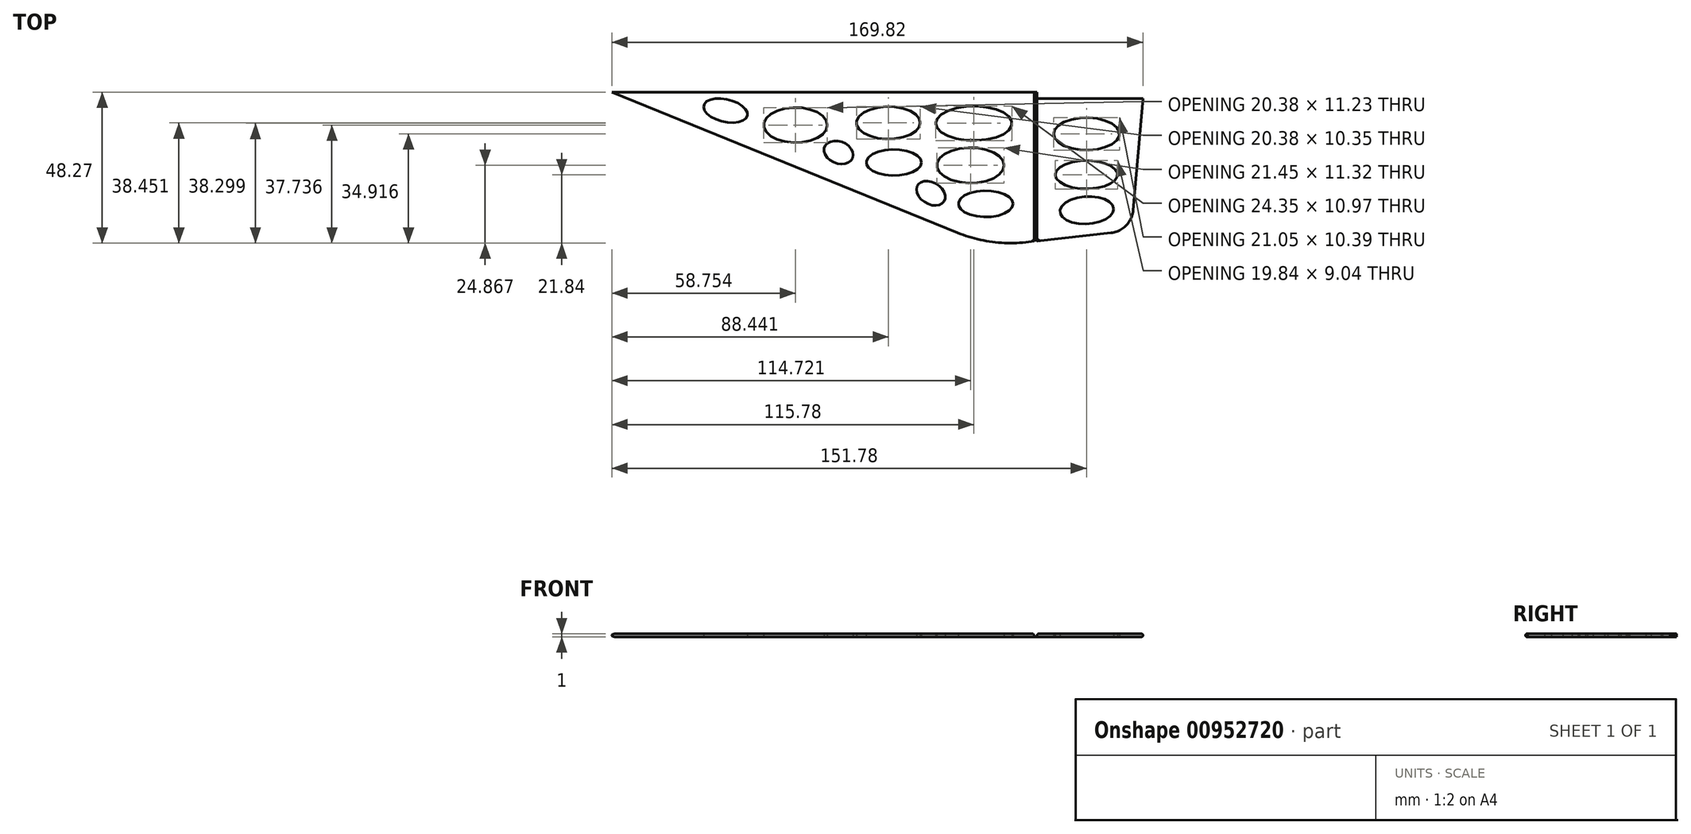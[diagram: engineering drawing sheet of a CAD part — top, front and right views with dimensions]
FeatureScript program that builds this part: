
annotation { "Feature Type Name" : "Feature", "Feature Type Description" : "" }
export const myFeature = defineFeature(function(context is Context, id is Id, definition is map)
    precondition{}
    {
        {
            var Q0;
            Q0=qCreatedBy(makeId("Top.planeOp"),FACE);
            var sketch = newSketch(context, id + "F0", { "sketchPlane" : qUnion([Q0])});
            skLineSegment(sketch, "E0", {"start": v(-90.21, 0) * mm, "end": v(44.79, 0) * mm});
            skLineSegment(sketch, "E1", {"start": v(76.47, -37.77) * mm, "end": v(79.61, -2) * mm});
            skLineSegment(sketch, "E2", {"start": v(-90.21, 0) * mm, "end": v(20.3, -44.95) * mm});
            skLineSegment(sketch, "E3", {"start": v(42.13, -48) * mm, "end": v(69.37, -45.03) * mm});
            skArc(sketch, "E4.filletArc", {"start": v(20.3, -44.95) * mm, "mid": v(31.02, -47.83) * mm, "end": v(42.13, -48) * mm});
            skArc(sketch, "E5.filletArc", {"start": v(69.37, -45.03) * mm, "mid": v(74.22, -42.67) * mm, "end": v(76.47, -37.77) * mm});
            skLineSegment(sketch, "E6", {"start": v(45.79, -2) * mm, "end": v(45.79, -47.6) * mm});
            skLineSegment(sketch, "E7.0", {"start": v(44.79, 0) * mm, "end": v(44.79, -47.7) * mm});
            skLineSegment(sketch, "E8.trimOffspring", {"start": v(45.79, -2) * mm, "end": v(79.61, -2) * mm});
            skPoint(sketch, "E9.orphan", {"position": v(45.79, 0) * mm});
            skPoint(sketch, "E10.orphan", {"position": v(79.79, 0) * mm});
            skLineSegment(sketch, "E11", {"start": v(44.79, 0) * mm, "end": v(45.79, 0) * mm});
            skLineSegment(sketch, "E12", {"start": v(45.79, -2) * mm, "end": v(45.79, 0) * mm});
            skEllipse(sketch, "E13", {"center": v(61.57, -13.35) * mm, "majorRadius": 10.52 * mm, "minorRadius": 5.2 * mm, "majorAxis": v(-1, 0)});
            skEllipse(sketch, "E14", {"center": v(61.57, -26.43) * mm, "majorRadius": 9.92 * mm, "minorRadius": 4.52 * mm, "majorAxis": v(-1, 0)});
            skEllipse(sketch, "E15", {"center": v(61.65, -37.78) * mm, "majorRadius": 8.57 * mm, "minorRadius": 4.4 * mm, "majorAxis": v(1, 0.06)});
            skEllipse(sketch, "E16", {"center": v(25.57, -9.97) * mm, "majorRadius": 12.18 * mm, "minorRadius": 5.48 * mm, "majorAxis": v(-1, 0)});
            skEllipse(sketch, "E17", {"center": v(24.51, -23.4) * mm, "majorRadius": 10.73 * mm, "minorRadius": 5.66 * mm, "majorAxis": v(1, 0)});
            skEllipse(sketch, "E18", {"center": v(29.34, -35.74) * mm, "majorRadius": 8.76 * mm, "minorRadius": 4.21 * mm, "majorAxis": v(1, 0)});
            skEllipse(sketch, "E19", {"center": v(-1.77, -9.82) * mm, "majorRadius": 10.2 * mm, "minorRadius": 5.17 * mm, "majorAxis": v(1, 0)});
            skEllipse(sketch, "E20", {"center": v(0, -22.5) * mm, "majorRadius": 8.82 * mm, "minorRadius": 4.16 * mm, "majorAxis": v(1, 0)});
            skEllipse(sketch, "E21", {"center": v(11.82, -32.34) * mm, "majorRadius": 4.98 * mm, "minorRadius": 3.47 * mm, "majorAxis": v(0.85, -0.52)});
            skEllipse(sketch, "E22", {"center": v(-31.46, -10.53) * mm, "majorRadius": 10.2 * mm, "minorRadius": 5.62 * mm, "majorAxis": v(1, 0)});
            skEllipse(sketch, "E23", {"center": v(-17.68, -19.3) * mm, "majorRadius": 4.81 * mm, "minorRadius": 3.52 * mm, "majorAxis": v(0.93, -0.37)});
            skEllipse(sketch, "E24", {"center": v(-53.82, -5.89) * mm, "majorRadius": 7.16 * mm, "minorRadius": 3.62 * mm, "majorAxis": v(0.97, -0.22)});
            skSolve(sketch);
        }
        {
            var Q0;
            Q0=makeQuery(id+"F0.imprint","IMPRINT",FACE,{"disambiguationData":[TD([[makeQuery(id+"F0.imprint","IMPRINT",EDGE,{"derivedFrom":sQuery(id+"F0.wireOp",EDGE,"E0")}),-1.0]])]});
            var Q1;
            {var subQ0=sQuery(id+"F0.wireOp",EDGE,"E6");Q1=makeQuery(id+"F0.imprint","IMPRINT",FACE,{"disambiguationData":[TD([[makeQuery(id+"F0.imprint","IMPRINT",EDGE,{"derivedFrom":subQ0}),-1.0]])]});}
            var Q2;
            Q2=makeQuery(id+"F0.imprint","IMPRINT",FACE,{"disambiguationData":[TD([[makeQuery(id+"F0.imprint","IMPRINT",EDGE,{"derivedFrom":sQuery(id+"F0.wireOp",EDGE,"E1")}),1.0]])]});
            extrude(context, id + "F1", {"entities" : qUnion([Q0, Q1, Q2]), "depth" : 1 * mm, "offsetDistance" : 25 * mm});
        }
        {
            var Q0;
            {var subQ0=sQuery(id+"F0.wireOp",EDGE,"E6");Q0=makeQuery(id+"F0.imprint","IMPRINT",FACE,{"disambiguationData":[TD([[makeQuery(id+"F0.imprint","IMPRINT",EDGE,{"derivedFrom":subQ0}),-1.0]])]});}
            extrude(context, id + "F2", {"entities" : qUnion([Q0]), "operationType" : NewBodyOperationType.REMOVE, "depth" : 2 * mm, "offsetDistance" : 25 * mm, "hasSecondDirection" : true, "secondDirectionOppositeDirection" : false, "secondDirectionDepth" : 0.15 * mm});
        }
        {
            var Q0;
            Q0=makeQuery(id+"F1.opExtrude","CAP_EDGE",EDGE,{"disambiguationData":[OSD([sQuery(id+"F0.wireOp",EDGE,"E2")])],"isStart":true});
            var Q1;
            Q1=makeQuery(id+"F1.opExtrude","CAP_EDGE",EDGE,{"disambiguationData":[OSD([sQuery(id+"F0.wireOp",EDGE,"E2")])],"isStart":false});
            var Q2;
            Q2=makeQuery(id+"F2.boolean.opBoolean","INTERSECT",EDGE,{"derivedFrom":[makeQuery(id+"F1.opExtrude","CAP_FACE",FACE,{"disambiguationData":[OSD([sQuery(id+"F0.wireOp",EDGE,"E0"),sQuery(id+"F0.wireOp",EDGE,"E1"),sQuery(id+"F0.wireOp",EDGE,"E2"),sQuery(id+"F0.wireOp",EDGE,"E3"),sQuery(id+"F0.wireOp",EDGE,"E4.filletArc"),sQuery(id+"F0.wireOp",EDGE,"E5.filletArc"),sQuery(id+"F0.wireOp",EDGE,"E8.trimOffspring"),sQuery(id+"F0.wireOp",EDGE,"E11"),sQuery(id+"F0.wireOp",EDGE,"E12"),sQuery(id+"F0.wireOp",EDGE,"E13"),sQuery(id+"F0.wireOp",EDGE,"E14"),sQuery(id+"F0.wireOp",EDGE,"E15"),sQuery(id+"F0.wireOp",EDGE,"E16"),sQuery(id+"F0.wireOp",EDGE,"E17"),sQuery(id+"F0.wireOp",EDGE,"E18"),sQuery(id+"F0.wireOp",EDGE,"E19"),sQuery(id+"F0.wireOp",EDGE,"E20"),sQuery(id+"F0.wireOp",EDGE,"E21"),sQuery(id+"F0.wireOp",EDGE,"E22"),sQuery(id+"F0.wireOp",EDGE,"E23"),sQuery(id+"F0.wireOp",EDGE,"E24")])],"isStart":false}),makeQuery(id+"F2.opExtrude","SWEPT_FACE",FACE,{"disambiguationData":[OSD([sQuery(id+"F0.wireOp",EDGE,"E7.0")])]})]});
            var Q3;
            {var subQ0=sQuery(id+"F0.wireOp",EDGE,"E12");Q3=makeQuery(id+"F2.boolean.opBoolean","INTERSECT",EDGE,{"derivedFrom":[makeQuery(id+"F1.opExtrude","CAP_FACE",FACE,{"disambiguationData":[OSD([sQuery(id+"F0.wireOp",EDGE,"E0"),sQuery(id+"F0.wireOp",EDGE,"E1"),sQuery(id+"F0.wireOp",EDGE,"E2"),sQuery(id+"F0.wireOp",EDGE,"E3"),sQuery(id+"F0.wireOp",EDGE,"E4.filletArc"),sQuery(id+"F0.wireOp",EDGE,"E5.filletArc"),sQuery(id+"F0.wireOp",EDGE,"E8.trimOffspring"),sQuery(id+"F0.wireOp",EDGE,"E11"),subQ0,sQuery(id+"F0.wireOp",EDGE,"E13"),sQuery(id+"F0.wireOp",EDGE,"E14"),sQuery(id+"F0.wireOp",EDGE,"E15"),sQuery(id+"F0.wireOp",EDGE,"E16"),sQuery(id+"F0.wireOp",EDGE,"E17"),sQuery(id+"F0.wireOp",EDGE,"E18"),sQuery(id+"F0.wireOp",EDGE,"E19"),sQuery(id+"F0.wireOp",EDGE,"E20"),sQuery(id+"F0.wireOp",EDGE,"E21"),sQuery(id+"F0.wireOp",EDGE,"E22"),sQuery(id+"F0.wireOp",EDGE,"E23"),sQuery(id+"F0.wireOp",EDGE,"E24")])],"isStart":false}),makeQuery(id+"F2.opExtrude","SWEPT_FACE",FACE,{"disambiguationData":[OSD([sQuery(id+"F0.wireOp",EDGE,"E6"),subQ0])]})]});}
            var Q4;
            {var subQ1=sQuery(id+"F0.wireOp",EDGE,"E5.filletArc");var subQ2=sQuery(id+"F0.wireOp",EDGE,"E3");Q4=makeQuery(id+"F2.boolean.opBoolean","SPLIT",EDGE,{"disambiguationData":[TD([makeQuery(id+"F1.opExtrude","SWEPT_FACE",FACE,{"disambiguationData":[OSD([subQ1])]})])],"derivedFrom":makeQuery(id+"F1.opExtrude","CAP_EDGE",EDGE,{"disambiguationData":[OSD([subQ2])],"isStart":false})});}
            fillet(context, id + "F3", {"entities" : qUnion([Q0, Q1, Q2, Q3, Q4]), "radius" : 0.5 * mm, "tangentPropagation" : true, "allowEdgeOverflow" : false});
        }
    });
